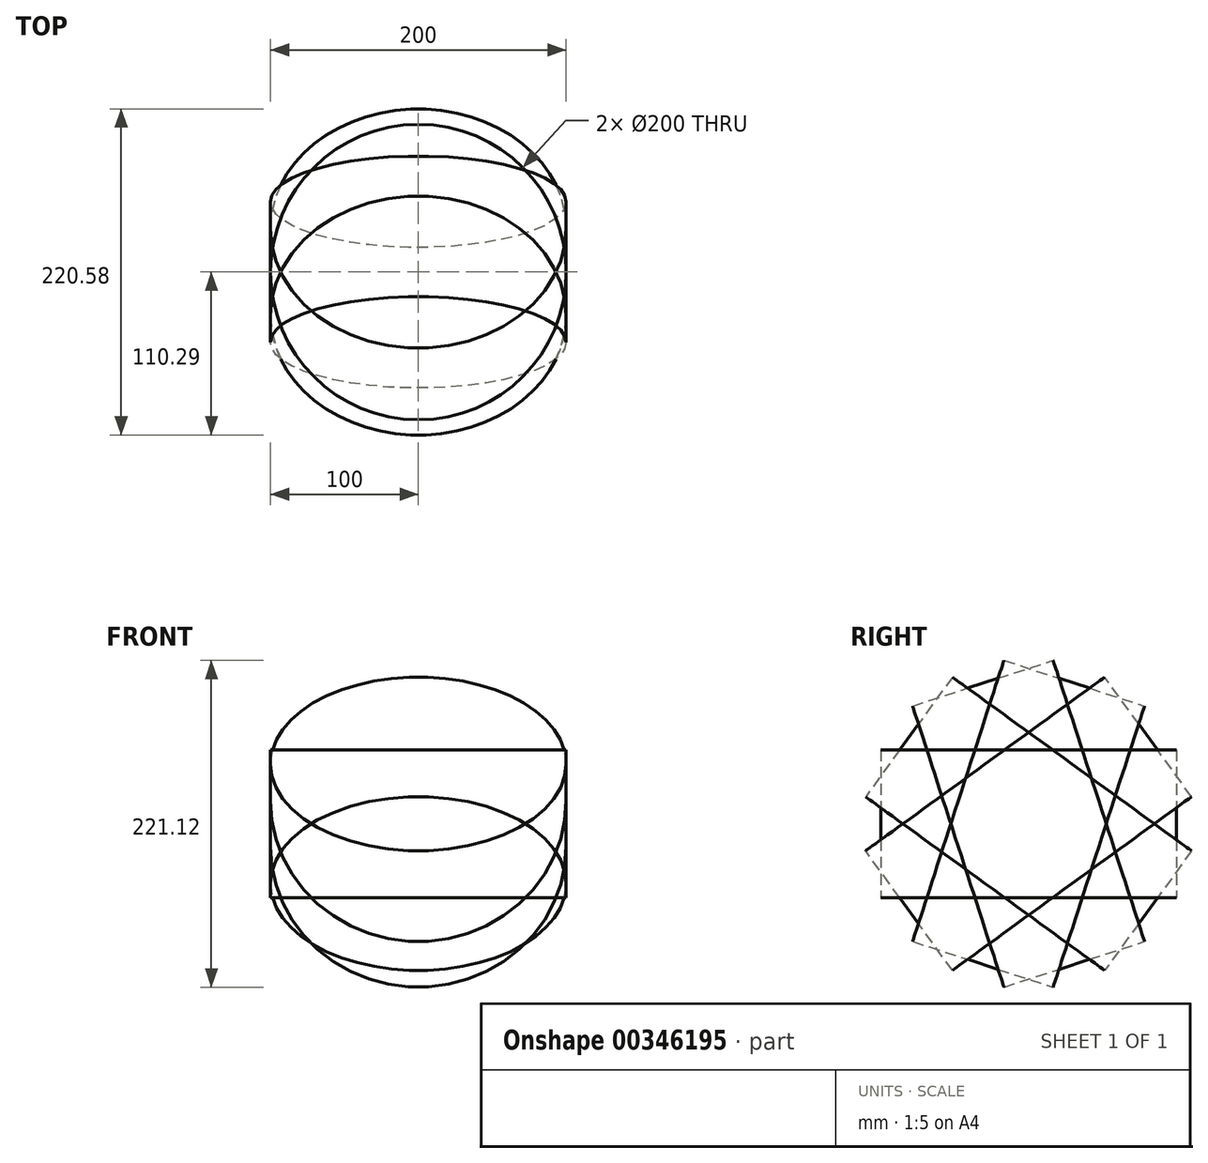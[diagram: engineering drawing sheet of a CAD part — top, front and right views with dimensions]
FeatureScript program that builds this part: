
annotation { "Feature Type Name" : "Feature", "Feature Type Description" : "" }
export const myFeature = defineFeature(function(context is Context, id is Id, definition is map)
    precondition{}
    {
        {
            var Q0;
            Q0=qCreatedBy(makeId("Front.planeOp"),FACE);
            var sketch = newSketch(context, id + "F0", { "sketchPlane" : qUnion([Q0])});
            skLineSegment(sketch, "E0.bottom", {"start": v(50, -50) * mm, "end": v(-50, -50) * mm});
            skLineSegment(sketch, "E0.top", {"start": v(50, 50) * mm, "end": v(-50, 50) * mm});
            skLineSegment(sketch, "E0.left", {"start": v(50, -50) * mm, "end": v(50, 50) * mm});
            skLineSegment(sketch, "E0.right", {"start": v(-50, -50) * mm, "end": v(-50, 50) * mm});
            skPoint(sketch, "E0.middle", {"position": v(0, 0) * mm});
            skSolve(sketch);
        }
        {
            var Q0;
            Q0=makeQuery(id+"F0.imprint","IMPRINT",FACE,{"disambiguationData":[TD([[makeQuery(id+"F0.imprint","IMPRINT",EDGE,{"derivedFrom":sQuery(id+"F0.wireOp",EDGE,"E0.bottom")}),-1.0]])]});
            var Q1;
            Q1=sQuery(id+"F0.wireOp",EDGE,"E0.left");
            var Q2;
            Q2=sQuery(id+"F0.wireOp",EDGE,"E0.right");
            revolve(context, id + "F1", {"bodyType" : ToolBodyType.SURFACE, "entities" : qUnion([Q0]), "surfaceEntities" : qUnion([Q1]), "axis" : qUnion([Q2]), "revolveType" : RevolveType.FULL});
        }
        {
            var Q0;
            Q0=qCreatedBy(makeId("Front.planeOp"),FACE);
            var sketch = newSketch(context, id + "F2", { "sketchPlane" : qUnion([Q0])});
            skLineSegment(sketch, "E1", {"start": v(0, 0) * mm, "end": v(154.53, 0) * mm});
            skSolve(sketch);
        }
        {
            var Q0;
            Q0=makeQuery(id+"F1.opRevolve","SWEPT_BODY",BODY,{"disambiguationData":[OSD([sQuery(id+"F0.wireOp",EDGE,"E0.left")])]});
            var Q1;
            Q1=makeQuery(id+"F84wM3Cg9SNBuYi_1.opPattern","COPY",BODY,{"derivedFrom":makeQuery(id+"F1.opRevolve","SWEPT_BODY",BODY,{"disambiguationData":[OSD([sQuery(id+"F0.wireOp",EDGE,"E0.left")])]}),"instanceName":"1"});
            var Q2;
            Q2=makeQuery(id+"F84wM3Cg9SNBuYi_1.opPattern","COPY",BODY,{"derivedFrom":makeQuery(id+"F1.opRevolve","SWEPT_BODY",BODY,{"disambiguationData":[OSD([sQuery(id+"F0.wireOp",EDGE,"E0.left")])]}),"instanceName":"2"});
            var Q3;
            Q3=makeQuery(id+"F84wM3Cg9SNBuYi_1.opPattern","COPY",BODY,{"derivedFrom":makeQuery(id+"F1.opRevolve","SWEPT_BODY",BODY,{"disambiguationData":[OSD([sQuery(id+"F0.wireOp",EDGE,"E0.left")])]}),"instanceName":"4"});
            var Q4;
            Q4=makeQuery(id+"F84wM3Cg9SNBuYi_1.opPattern","COPY",BODY,{"derivedFrom":makeQuery(id+"F1.opRevolve","SWEPT_BODY",BODY,{"disambiguationData":[OSD([sQuery(id+"F0.wireOp",EDGE,"E0.left")])]}),"instanceName":"3"});
            var Q5;
            Q5=makeQuery(id+"F84wM3Cg9SNBuYi_1.opPattern","COPY",BODY,{"derivedFrom":makeQuery(id+"F1.opRevolve","SWEPT_BODY",BODY,{"disambiguationData":[OSD([sQuery(id+"F0.wireOp",EDGE,"E0.left")])]}),"instanceName":"5"});
            var Q6;
            Q6=makeQuery(id+"F84wM3Cg9SNBuYi_1.opPattern","COPY",BODY,{"derivedFrom":makeQuery(id+"F1.opRevolve","SWEPT_BODY",BODY,{"disambiguationData":[OSD([sQuery(id+"F0.wireOp",EDGE,"E0.left")])]}),"instanceName":"6"});
            var Q7;
            Q7=makeQuery(id+"F84wM3Cg9SNBuYi_1.opPattern","COPY",BODY,{"derivedFrom":makeQuery(id+"F1.opRevolve","SWEPT_BODY",BODY,{"disambiguationData":[OSD([sQuery(id+"F0.wireOp",EDGE,"E0.left")])]}),"instanceName":"7"});
            var Q8;
            Q8=makeQuery(id+"F84wM3Cg9SNBuYi_1.opPattern","COPY",BODY,{"derivedFrom":makeQuery(id+"F1.opRevolve","SWEPT_BODY",BODY,{"disambiguationData":[OSD([sQuery(id+"F0.wireOp",EDGE,"E0.left")])]}),"instanceName":"0_7"});
            var Q9;
            Q9=makeQuery(id+"F84wM3Cg9SNBuYi_1.opPattern","COPY",BODY,{"derivedFrom":makeQuery(id+"F1.opRevolve","SWEPT_BODY",BODY,{"disambiguationData":[OSD([sQuery(id+"F0.wireOp",EDGE,"E0.left")])]}),"instanceName":"2_7"});
            var Q10;
            Q10=makeQuery(id+"F84wM3Cg9SNBuYi_1.opPattern","COPY",BODY,{"derivedFrom":makeQuery(id+"F1.opRevolve","SWEPT_BODY",BODY,{"disambiguationData":[OSD([sQuery(id+"F0.wireOp",EDGE,"E0.left")])]}),"instanceName":"1_7"});
            var Q11;
            Q11=makeQuery(id+"F84wM3Cg9SNBuYi_1.opPattern","COPY",BODY,{"derivedFrom":makeQuery(id+"F1.opRevolve","SWEPT_BODY",BODY,{"disambiguationData":[OSD([sQuery(id+"F0.wireOp",EDGE,"E0.left")])]}),"instanceName":"3_7"});
            var Q12;
            Q12=makeQuery(id+"F84wM3Cg9SNBuYi_1.opPattern","COPY",BODY,{"derivedFrom":makeQuery(id+"F1.opRevolve","SWEPT_BODY",BODY,{"disambiguationData":[OSD([sQuery(id+"F0.wireOp",EDGE,"E0.left")])]}),"instanceName":"5_7"});
            var Q13;
            Q13=makeQuery(id+"F84wM3Cg9SNBuYi_1.opPattern","COPY",BODY,{"derivedFrom":makeQuery(id+"F1.opRevolve","SWEPT_BODY",BODY,{"disambiguationData":[OSD([sQuery(id+"F0.wireOp",EDGE,"E0.left")])]}),"instanceName":"4_7"});
            var Q14;
            Q14=makeQuery(id+"F84wM3Cg9SNBuYi_1.opPattern","COPY",BODY,{"derivedFrom":makeQuery(id+"F1.opRevolve","SWEPT_BODY",BODY,{"disambiguationData":[OSD([sQuery(id+"F0.wireOp",EDGE,"E0.left")])]}),"instanceName":"7_7"});
            var Q15;
            Q15=makeQuery(id+"F84wM3Cg9SNBuYi_1.opPattern","COPY",BODY,{"derivedFrom":makeQuery(id+"F1.opRevolve","SWEPT_BODY",BODY,{"disambiguationData":[OSD([sQuery(id+"F0.wireOp",EDGE,"E0.left")])]}),"instanceName":"6_7"});
            var Q16;
            Q16=sQuery(id+"F2.wireOp",EDGE,"E1");
            circularPattern(context, id + "F3", {"entities" : qUnion([Q0, Q1, Q2, Q3, Q4, Q5, Q6, Q7, Q8, Q9, Q10, Q11, Q12, Q13, Q14, Q15]), "axis" : qUnion([Q16]), "angle" : 360 * degree, "instanceCount" : 10, "equalSpace" : true});
        }
    });
